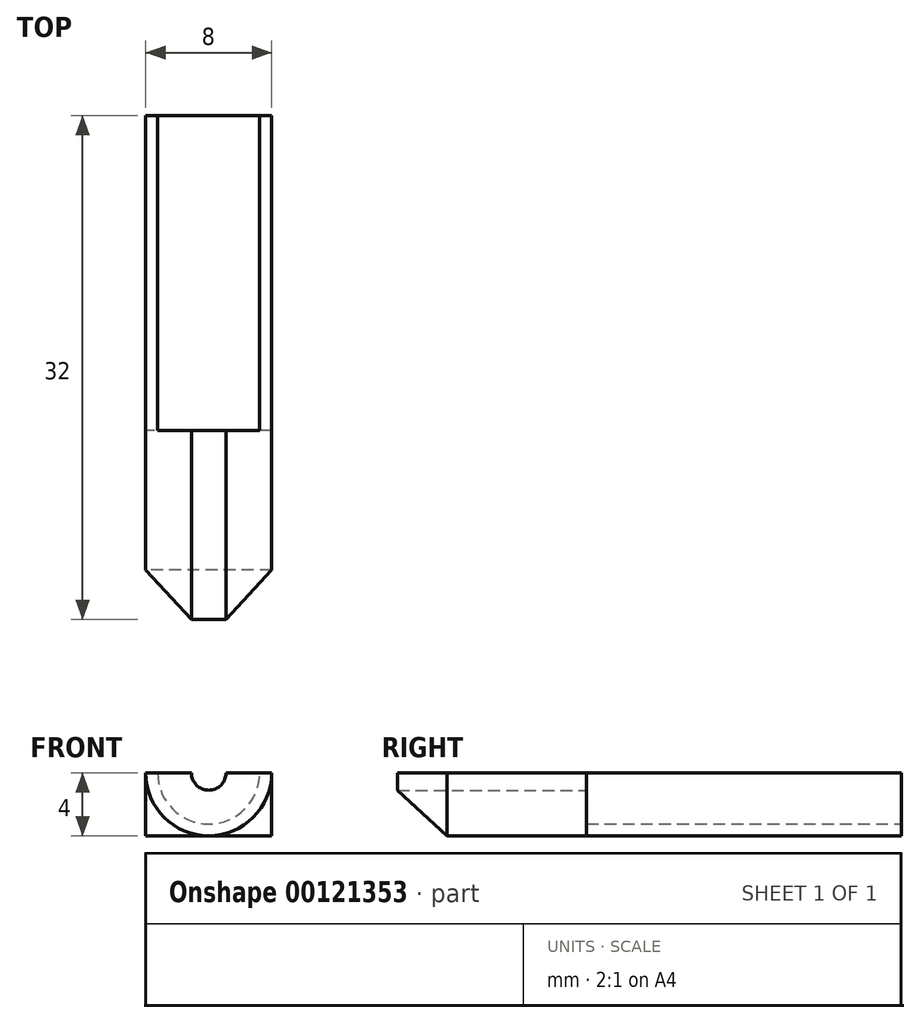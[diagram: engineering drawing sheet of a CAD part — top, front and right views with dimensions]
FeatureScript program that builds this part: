
annotation { "Feature Type Name" : "Feature", "Feature Type Description" : "" }
export const myFeature = defineFeature(function(context is Context, id is Id, definition is map)
    precondition{}
    {
        {
            var Q0;
            Q0=qCreatedBy(makeId("Top.planeOp"),FACE);
            var sketch = newSketch(context, id + "F0", { "sketchPlane" : qUnion([Q0])});
            skLineSegment(sketch, "E0", {"start": v(0, 20.85) * mm, "end": v(0, -12) * mm, "construction": true});
            skLineSegment(sketch, "E1", {"start": v(-4, 0) * mm, "end": v(7.04, 0) * mm, "construction": true});
            skLineSegment(sketch, "E2.0", {"start": v(-4.78, -12) * mm, "end": v(7.04, -12) * mm, "construction": true});
            skLineSegment(sketch, "E3.0", {"start": v(-1.1, 0) * mm, "end": v(-1.1, -12) * mm, "construction": true});
            skLineSegment(sketch, "E4.0", {"start": v(-1.55, 20.85) * mm, "end": v(-1.55, 0) * mm, "construction": true});
            skLineSegment(sketch, "E5.0", {"start": v(-4, 20.85) * mm, "end": v(-4, -12) * mm, "construction": true});
            skLineSegment(sketch, "E6", {"start": v(-1.1, -12) * mm, "end": v(-4, -8.86) * mm});
            skLineSegment(sketch, "E7", {"start": v(-4, -8.86) * mm, "end": v(-4, 0) * mm});
            skLineSegment(sketch, "E8", {"start": v(-1.55, 0) * mm, "end": v(-1.1, 0) * mm});
            skLineSegment(sketch, "E9", {"start": v(-1.1, -12) * mm, "end": v(-1.1, 0) * mm});
            skPoint(sketch, "E10.orphan", {"position": v(-4.78, 0) * mm});
            skLineSegment(sketch, "E11.0", {"start": v(-4, 20) * mm, "end": v(7.04, 20) * mm, "construction": true});
            skLineSegment(sketch, "E12.0", {"start": v(-4, 5) * mm, "end": v(7.04, 5) * mm, "construction": true});
            skLineSegment(sketch, "E13", {"start": v(-4, 0) * mm, "end": v(-1.1, 0) * mm});
            skLineSegment(sketch, "E14", {"start": v(-1.55, 5) * mm, "end": v(-4, 5) * mm});
            skLineSegment(sketch, "E15", {"start": v(-4, 0) * mm, "end": v(-4, 5) * mm});
            skLineSegment(sketch, "E16", {"start": v(-1.55, 5) * mm, "end": v(-1.55, 0) * mm});
            skLineSegment(sketch, "E17", {"start": v(-3.24, 5) * mm, "end": v(-3.24, 0) * mm});
            skLineSegment(sketch, "E18.0", {"start": v(-4, 14) * mm, "end": v(7.04, 14) * mm, "construction": true});
            skLineSegment(sketch, "E19", {"start": v(-3.24, 5) * mm, "end": v(-3.24, 14) * mm});
            skLineSegment(sketch, "E20", {"start": v(-3.24, 14) * mm, "end": v(-4, 14) * mm});
            skLineSegment(sketch, "E21", {"start": v(-4, 5) * mm, "end": v(-4, 14) * mm});
            skLineSegment(sketch, "E22", {"start": v(-3.24, 14) * mm, "end": v(-3.24, 20) * mm});
            skLineSegment(sketch, "E23", {"start": v(-3.24, 20) * mm, "end": v(-1.55, 20) * mm});
            skLineSegment(sketch, "E24", {"start": v(-1.55, 20) * mm, "end": v(-1.55, 14) * mm});
            skLineSegment(sketch, "E25", {"start": v(-1.55, 14) * mm, "end": v(-3.24, 14) * mm});
            skLineSegment(sketch, "E26", {"start": v(-3.24, 20) * mm, "end": v(-4, 20) * mm});
            skLineSegment(sketch, "E27", {"start": v(-4, 14) * mm, "end": v(-4, 20) * mm});
            skSolve(sketch);
        }
        {
            var Q0;
            Q0=makeQuery(id+"F0.imprint","IMPRINT",FACE,{"disambiguationData":[TD([[makeQuery(id+"F0.imprint","IMPRINT",EDGE,{"derivedFrom":sQuery(id+"F0.wireOp",EDGE,"E6")}),-1.0]])]});
            var Q1;
            {var subQ0=sQuery(id+"F0.wireOp",EDGE,"E15");Q1=makeQuery(id+"F0.imprint","IMPRINT",FACE,{"disambiguationData":[TD([[makeQuery(id+"F0.imprint","IMPRINT",EDGE,{"derivedFrom":subQ0}),-1.0]])]});}
            var Q2;
            {var subQ2=sQuery(id+"F0.wireOp",EDGE,"E19");Q2=makeQuery(id+"F0.imprint","IMPRINT",FACE,{"disambiguationData":[TD([[makeQuery(id+"F0.imprint","IMPRINT",EDGE,{"derivedFrom":subQ2}),1.0]])]});}
            var Q3;
            Q3=makeQuery(id+"F0.imprint","IMPRINT",FACE,{"disambiguationData":[TD([[makeQuery(id+"F0.imprint","IMPRINT",EDGE,{"derivedFrom":sQuery(id+"F0.wireOp",EDGE,"E20")}),-1.0]])]});
            var Q4;
            Q4=sQuery(id+"F0.wireOp",EDGE,"E0");
            revolve(context, id + "F1", {"entities" : qUnion([Q0, Q1, Q2, Q3]), "axis" : qUnion([Q4]), "revolveType" : RevolveType.ONE_DIRECTION, "angle" : 180 * degree});
        }
        {
            var Q0;
            Q0=makeQuery(id+"FP6nejvB5zhyoSZ_0.boolean.opBoolean","MERGE",FACE,{"derivedFrom":[makeQuery(id+"F1.opRevolve","SWEPT_FACE",FACE,{"disambiguationData":[OSD([sQuery(id+"F0.wireOp",EDGE,"E26")])]}),makeQuery(id+"FP6nejvB5zhyoSZ_0.opRevolve","SWEPT_FACE",FACE,{"disambiguationData":[OSD([sQuery(id+"F0.wireOp",EDGE,"E23")])]})]});
            var sketch = newSketch(context, id + "F2", { "sketchPlane" : qUnion([Q0])});
            skArc(sketch, "E28.0.0", {"start": v(-4, 0) * mm, "mid": v(0, -4) * mm, "end": v(4, 0) * mm});
            skLineSegment(sketch, "E28.0.1", {"start": v(4, 0) * mm, "end": v(3.24, 0) * mm});
            skArc(sketch, "E28.0.2", {"start": v(3.24, 0) * mm, "mid": v(0, 3.24) * mm, "end": v(-3.24, 0) * mm});
            skLineSegment(sketch, "E28.0.3", {"start": v(-3.24, 0) * mm, "end": v(-4, 0) * mm});
            skLineSegment(sketch, "E29", {"start": v(-4, 0) * mm, "end": v(-4, -4) * mm});
            skPoint(sketch, "E29.endSnap0", {"position": v(0, -4) * mm});
            skLineSegment(sketch, "E30", {"start": v(-4, -4) * mm, "end": v(4, -4) * mm});
            skLineSegment(sketch, "E31", {"start": v(4, -4) * mm, "end": v(4, 0) * mm});
            skSolve(sketch);
        }
        {
            var Q0;
            {var subQ0=sQuery(id+"F2.wireOp",EDGE,"E29");Q0=makeQuery(id+"F2.imprint","IMPRINT",FACE,{"disambiguationData":[TD([[makeQuery(id+"F2.imprint","IMPRINT",EDGE,{"derivedFrom":subQ0}),1.0]])]});}
            var Q1;
            {var subQ0=sQuery(id+"F2.wireOp",EDGE,"E31");Q1=makeQuery(id+"F2.imprint","IMPRINT",FACE,{"disambiguationData":[TD([[makeQuery(id+"F2.imprint","IMPRINT",EDGE,{"derivedFrom":subQ0}),1.0]])]});}
            extrude(context, id + "F3", {"entities" : qUnion([Q0, Q1]), "operationType" : NewBodyOperationType.ADD, "oppositeDirection" : true, "depth" : 20 * mm});
        }
    });
